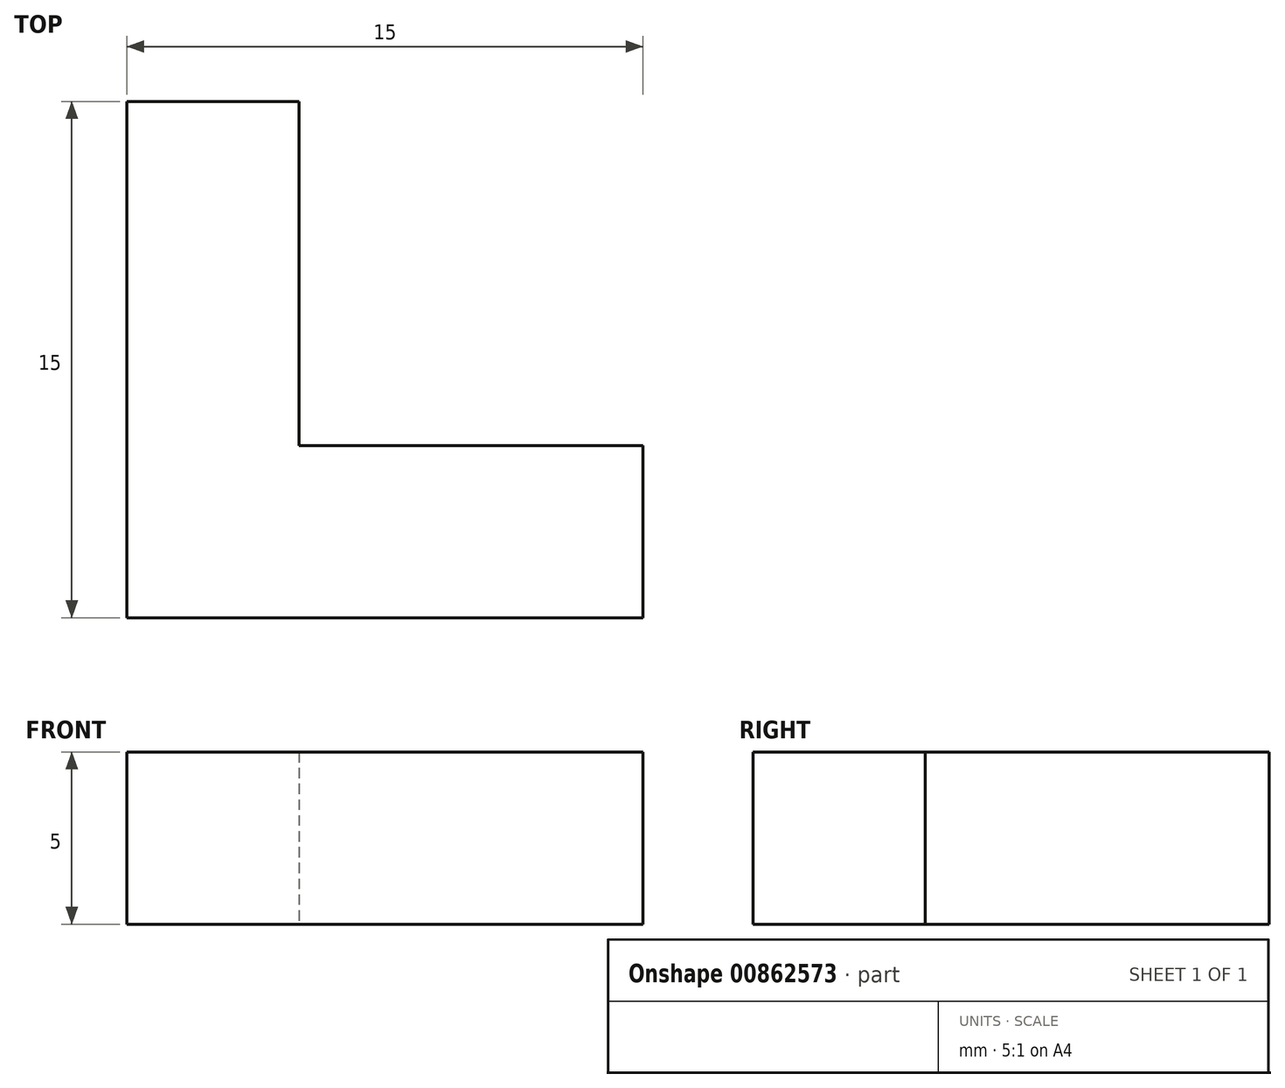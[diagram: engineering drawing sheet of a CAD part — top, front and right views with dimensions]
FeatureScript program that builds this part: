
annotation { "Feature Type Name" : "Feature", "Feature Type Description" : "" }
export const myFeature = defineFeature(function(context is Context, id is Id, definition is map)
    precondition{}
    {
        {
            var Q0;
            Q0=qCreatedBy(makeId("Top.planeOp"),FACE);
            var sketch = newSketch(context, id + "F0", { "sketchPlane" : qUnion([Q0])});
            skLineSegment(sketch, "E0", {"start": v(0, 0) * mm, "end": v(0, 15) * mm});
            skLineSegment(sketch, "E1", {"start": v(0, 15) * mm, "end": v(5, 15) * mm});
            skLineSegment(sketch, "E2", {"start": v(5, 15) * mm, "end": v(5, 5) * mm});
            skLineSegment(sketch, "E3", {"start": v(5, 5) * mm, "end": v(15, 5) * mm});
            skLineSegment(sketch, "E4", {"start": v(15, 5) * mm, "end": v(15, 0) * mm});
            skLineSegment(sketch, "E5", {"start": v(15, 0) * mm, "end": v(0, 0) * mm});
            skSolve(sketch);
        }
        {
            var Q0;
            Q0 = qSketchRegion(id + "F0", true);
            extrude(context, id + "F1", {"entities" : qUnion([Q0]), "depth" : 5 * mm, "offsetDistance" : 25 * mm});
        }
    });
